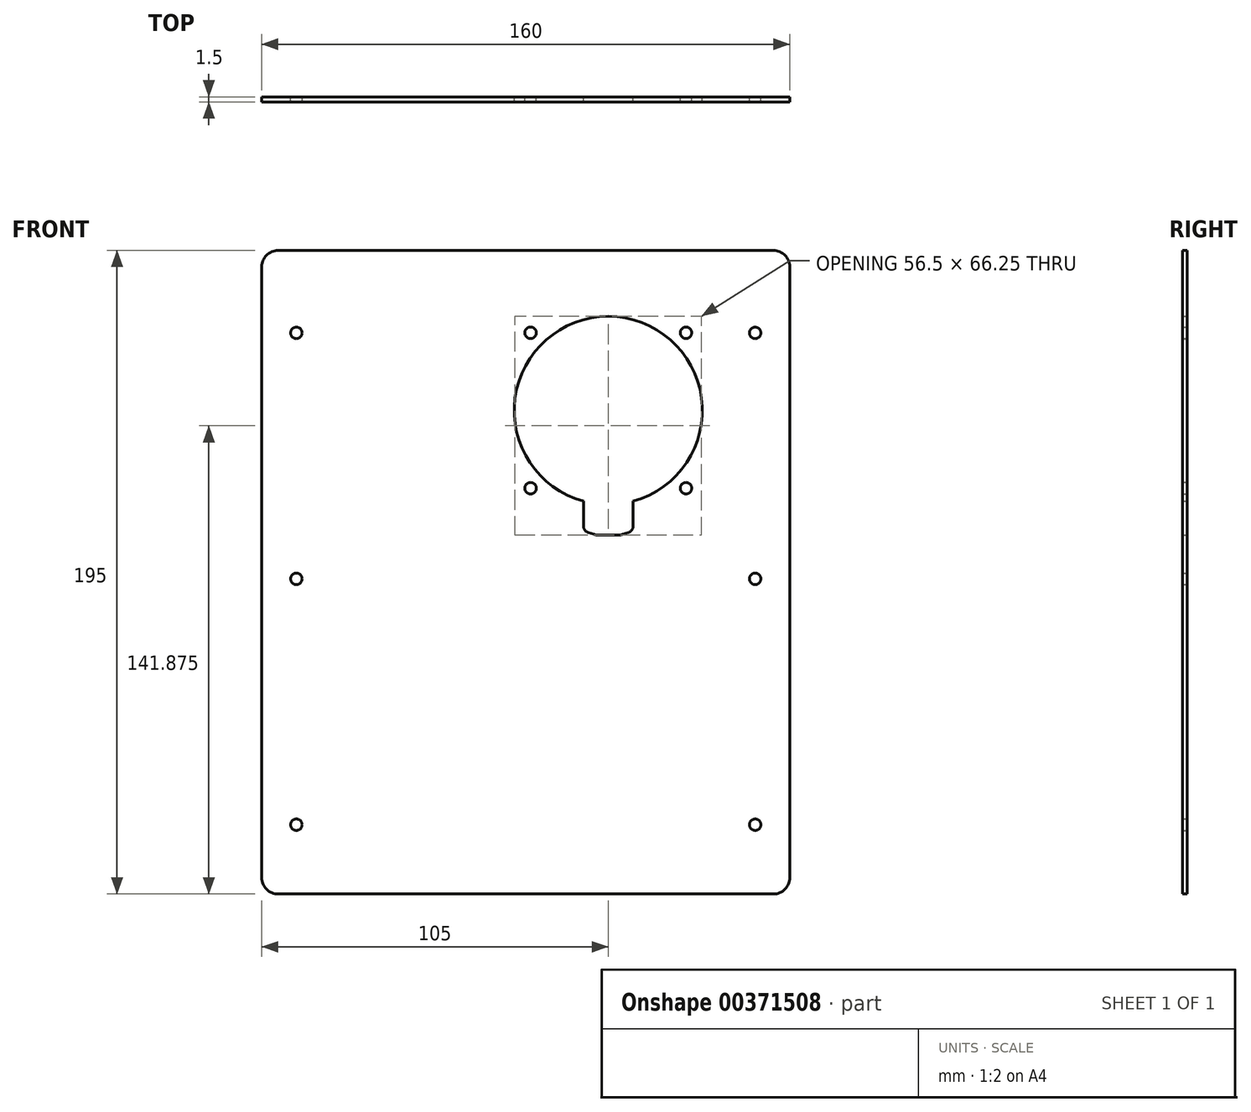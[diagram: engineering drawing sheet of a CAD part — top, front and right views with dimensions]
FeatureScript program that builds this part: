
annotation { "Feature Type Name" : "Feature", "Feature Type Description" : "" }
export const myFeature = defineFeature(function(context is Context, id is Id, definition is map)
    precondition{}
    {
        {
            var Q0;
            Q0=qCreatedBy(makeId("Front.planeOp"),FACE);
            var sketch = newSketch(context, id + "F0", { "sketchPlane" : qUnion([Q0])});
            skPoint(sketch, "E0.middle", {"position": v(0, 0) * mm});
            skCircle(sketch, "E1", {"center": v(0, 0) * mm, "radius": 33.3 * mm, "construction": true});
            skArc(sketch, "E2", {"start": v(7.5, -27.5) * mm, "mid": v(0, 28.5) * mm, "end": v(-7.5, -27.5) * mm});
            skLineSegment(sketch, "E3", {"start": v(-45.02, 0) * mm, "end": v(64.75, 0) * mm, "construction": true});
            skLineSegment(sketch, "E4", {"start": v(0, -38.5) * mm, "end": v(0, 68.67) * mm, "construction": true});
            skLineSegment(sketch, "E5", {"start": v(0, 0) * mm, "end": v(0, 0) * mm});
            skCircle(sketch, "E6", {"center": v(-23.55, 23.55) * mm, "radius": 1.75 * mm});
            skLineSegment(sketch, "E7", {"start": v(-23.55, 23.55) * mm, "end": v(0, 0) * mm, "construction": true});
            skCircle(sketch, "E8.1.0", {"center": v(-23.55, -23.55) * mm, "radius": 1.75 * mm});
            skCircle(sketch, "E8.2.0", {"center": v(23.55, -23.55) * mm, "radius": 1.75 * mm});
            skCircle(sketch, "E9.1.3.0", {"center": v(23.55, 23.55) * mm, "radius": 1.75 * mm});
            skLineSegment(sketch, "E10", {"start": v(0, 0) * mm, "end": v(23.55, 23.55) * mm, "construction": true});
            skLineSegment(sketch, "E11", {"start": v(0, 0) * mm, "end": v(23.55, -23.55) * mm, "construction": true});
            skLineSegment(sketch, "E12", {"start": v(0, 0) * mm, "end": v(-23.55, -23.55) * mm, "construction": true});
            skLineSegment(sketch, "E13", {"start": v(55, 48.5) * mm, "end": v(-105, 48.5) * mm});
            skLineSegment(sketch, "E14", {"start": v(-105, 48.5) * mm, "end": v(-105, -146.5) * mm});
            skLineSegment(sketch, "E15", {"start": v(-105, -146.5) * mm, "end": v(55, -146.5) * mm});
            skLineSegment(sketch, "E16", {"start": v(55, 48.5) * mm, "end": v(55, -146.5) * mm});
            skLineSegment(sketch, "E17", {"start": v(0, -37.75) * mm, "end": v(-3.75, -37.75) * mm});
            skLineSegment(sketch, "E18", {"start": v(-7.5, -36.5) * mm, "end": v(-7.5, -30) * mm});
            skLineSegment(sketch, "E19.MirrorCS", {"start": v(0, -37.75) * mm, "end": v(3.75, -37.75) * mm});
            skLineSegment(sketch, "E20.MirrorCS", {"start": v(7.5, -36.5) * mm, "end": v(7.5, -30) * mm});
            skLineSegment(sketch, "E21", {"start": v(-7.5, -30) * mm, "end": v(-7.5, -27.5) * mm});
            skLineSegment(sketch, "E22", {"start": v(7.5, -30) * mm, "end": v(7.5, -27.5) * mm});
            skLineSegment(sketch, "E23", {"start": v(-3.75, -37.75) * mm, "end": v(-7.5, -36.5) * mm});
            skPoint(sketch, "E24.orphan", {"position": v(-7.5, -37.75) * mm});
            skLineSegment(sketch, "E25.MirrorCS", {"start": v(3.75, -37.75) * mm, "end": v(7.5, -36.5) * mm});
            skLineSegment(sketch, "E26", {"start": v(-25, 57.8) * mm, "end": v(-25, -159.57) * mm, "construction": true});
            skLineSegment(sketch, "E27", {"start": v(-94.5, 58.24) * mm, "end": v(-94.5, -173.22) * mm, "construction": true});
            skCircle(sketch, "E28", {"center": v(-94.5, 23.5) * mm, "radius": 1.75 * mm});
            skCircle(sketch, "E29", {"center": v(-94.5, -51) * mm, "radius": 1.75 * mm});
            skCircle(sketch, "E30", {"center": v(-94.5, -125.5) * mm, "radius": 1.75 * mm});
            skLineSegment(sketch, "E31.MirrorCS", {"start": v(44.5, 58.24) * mm, "end": v(44.5, -173.22) * mm, "construction": true});
            skCircle(sketch, "E32.MirrorC", {"center": v(44.5, 23.5) * mm, "radius": 1.75 * mm});
            skCircle(sketch, "E33.MirrorC", {"center": v(44.5, -51) * mm, "radius": 1.75 * mm});
            skCircle(sketch, "E34.MirrorC", {"center": v(44.5, -125.5) * mm, "radius": 1.75 * mm});
            skSolve(sketch);
        }
        {
            var Q0;
            Q0=makeQuery(id+"F0.imprint","IMPRINT",FACE,{"disambiguationData":[TD([[makeQuery(id+"F0.imprint","IMPRINT",EDGE,{"derivedFrom":sQuery(id+"F0.wireOp",EDGE,"E13")}),1.0]])]});
            extrude(context, id + "F1", {"entities" : qUnion([Q0]), "depth" : 1.5 * mm, "offsetDistance" : 25 * mm});
        }
        {
            var Q0;
            Q0=makeQuery(id+"F1.opExtrude","SWEPT_EDGE",EDGE,{"disambiguationData":[OSD([sQuery(id+"F0.wireOp",EDGE,"E20.MirrorCS"),sQuery(id+"F0.wireOp",EDGE,"E25.MirrorCS")])]});
            var Q1;
            Q1=makeQuery(id+"F1.opExtrude","SWEPT_EDGE",EDGE,{"disambiguationData":[OSD([sQuery(id+"F0.wireOp",EDGE,"E18"),sQuery(id+"F0.wireOp",EDGE,"E23")])]});
            fillet(context, id + "F2", {"entities" : qUnion([Q0, Q1]), "tangentPropagation" : true, "radius" : 2 * mm, "defaultsChanged" : false, "vertexSettings" : [], "allowEdgeOverflow" : false});
        }
        {
            var Q0;
            Q0=makeQuery(id+"F1.opExtrude","SWEPT_EDGE",EDGE,{"disambiguationData":[OSD([sQuery(id+"F0.wireOp",EDGE,"E19.MirrorCS"),sQuery(id+"F0.wireOp",EDGE,"E25.MirrorCS")])]});
            var Q1;
            Q1=makeQuery(id+"F1.opExtrude","SWEPT_EDGE",EDGE,{"disambiguationData":[OSD([sQuery(id+"F0.wireOp",EDGE,"E17"),sQuery(id+"F0.wireOp",EDGE,"E23")])]});
            fillet(context, id + "F3", {"entities" : qUnion([Q0, Q1]), "tangentPropagation" : true, "radius" : 4 * mm, "defaultsChanged" : true, "vertexSettings" : [], "allowEdgeOverflow" : false});
        }
        {
            var Q0;
            Q0=makeQuery(id+"F1.opExtrude","SWEPT_EDGE",EDGE,{"disambiguationData":[OSD([sQuery(id+"F0.wireOp",EDGE,"E13"),sQuery(id+"F0.wireOp",EDGE,"E16")])]});
            var Q1;
            Q1=makeQuery(id+"F1.opExtrude","SWEPT_EDGE",EDGE,{"disambiguationData":[OSD([sQuery(id+"F0.wireOp",EDGE,"E13"),sQuery(id+"F0.wireOp",EDGE,"E14")])]});
            var Q2;
            Q2=makeQuery(id+"F1.opExtrude","SWEPT_EDGE",EDGE,{"disambiguationData":[OSD([sQuery(id+"F0.wireOp",EDGE,"E14"),sQuery(id+"F0.wireOp",EDGE,"E15")])]});
            var Q3;
            Q3=makeQuery(id+"F1.opExtrude","SWEPT_EDGE",EDGE,{"disambiguationData":[OSD([sQuery(id+"F0.wireOp",EDGE,"E15"),sQuery(id+"F0.wireOp",EDGE,"E16")])]});
            fillet(context, id + "F4", {"entities" : qUnion([Q0, Q1, Q2, Q3]), "tangentPropagation" : true, "radius" : 5 * mm, "defaultsChanged" : false, "vertexSettings" : [], "allowEdgeOverflow" : false});
        }
    });
